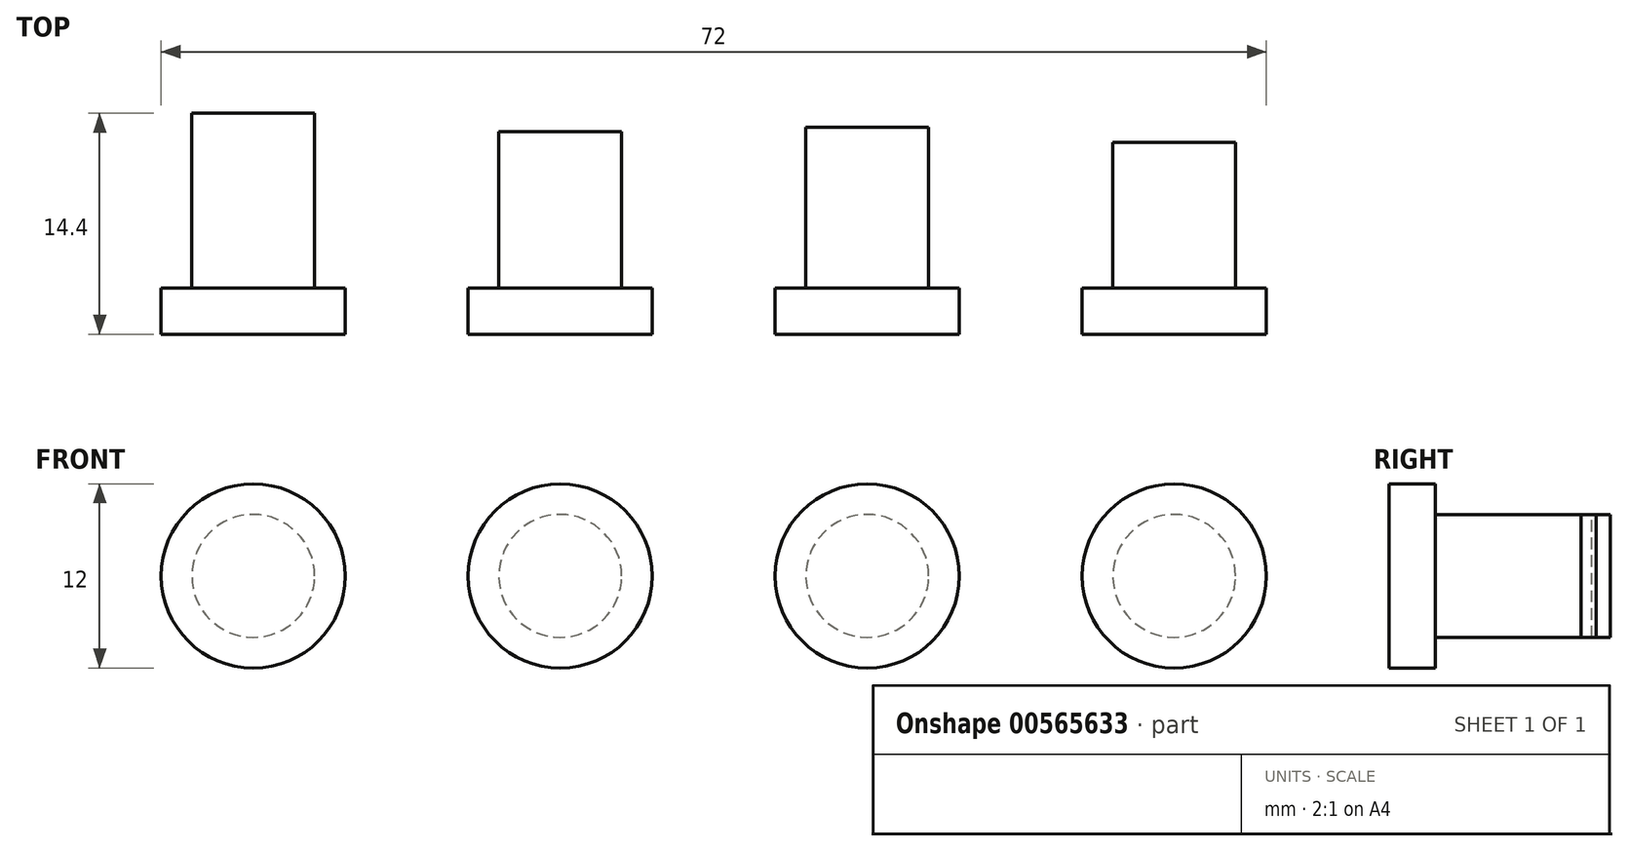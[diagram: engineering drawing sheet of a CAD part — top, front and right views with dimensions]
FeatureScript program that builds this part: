
annotation { "Feature Type Name" : "Feature", "Feature Type Description" : "" }
export const myFeature = defineFeature(function(context is Context, id is Id, definition is map)
    precondition{}
    {
        {
            var Q0;
            Q0=qCreatedBy(makeId("Front.planeOp"),FACE);
            var sketch = newSketch(context, id + "F0", { "sketchPlane" : qUnion([Q0])});
            skLineSegment(sketch, "E0", {"start": v(-7.35, 0) * mm, "end": v(7.35, 0) * mm, "construction": true});
            skLineSegment(sketch, "E1", {"start": v(0, 7.35) * mm, "end": v(0, -7.35) * mm, "construction": true});
            skPoint(sketch, "E2", {"position": v(0, 0) * mm});
            skCircle(sketch, "E3", {"center": v(0, 0) * mm, "radius": 4 * mm});
            skCircle(sketch, "E4", {"center": v(0, 0) * mm, "radius": 0.8 * mm, "construction": true});
            skLineSegment(sketch, "E5", {"start": v(18.77, 0) * mm, "end": v(101.23, 0) * mm, "construction": true});
            skLineSegment(sketch, "E6", {"start": v(60, 7.35) * mm, "end": v(60, -7.35) * mm, "construction": true});
            skPoint(sketch, "E7", {"position": v(60, 0) * mm});
            skCircle(sketch, "E8", {"center": v(60, 0) * mm, "radius": 4 * mm});
            skCircle(sketch, "E9", {"center": v(60, 0) * mm, "radius": 0.8 * mm, "construction": true});
            skLineSegment(sketch, "E10", {"start": v(9.1, 0) * mm, "end": v(70.9, 0) * mm, "construction": true});
            skLineSegment(sketch, "E11", {"start": v(40, 7.35) * mm, "end": v(40, -7.35) * mm, "construction": true});
            skPoint(sketch, "E12", {"position": v(40, 0) * mm});
            skCircle(sketch, "E13", {"center": v(40, 0) * mm, "radius": 4 * mm});
            skCircle(sketch, "E14", {"center": v(40, 0) * mm, "radius": 0.8 * mm, "construction": true});
            skLineSegment(sketch, "E15", {"start": v(7.93, 0) * mm, "end": v(32.07, 0) * mm, "construction": true});
            skLineSegment(sketch, "E16", {"start": v(20, 7.35) * mm, "end": v(20, -7.35) * mm, "construction": true});
            skPoint(sketch, "E17", {"position": v(20, 0) * mm});
            skCircle(sketch, "E18", {"center": v(20, 0) * mm, "radius": 4 * mm});
            skCircle(sketch, "E19", {"center": v(20, 0) * mm, "radius": 0.8 * mm, "construction": true});
            skLineSegment(sketch, "E20", {"start": v(0, 0) * mm, "end": v(20, 0) * mm, "construction": true});
            skLineSegment(sketch, "E21", {"start": v(20, 0) * mm, "end": v(40, 0) * mm, "construction": true});
            skLineSegment(sketch, "E22", {"start": v(40, 0) * mm, "end": v(60, 0) * mm, "construction": true});
            skCircle(sketch, "E23", {"center": v(0, 0) * mm, "radius": 6 * mm});
            skCircle(sketch, "E24", {"center": v(20, 0) * mm, "radius": 6 * mm});
            skCircle(sketch, "E25", {"center": v(40, 0) * mm, "radius": 6 * mm});
            skCircle(sketch, "E26", {"center": v(60, 0) * mm, "radius": 6 * mm});
            skSolve(sketch);
        }
        {
            var Q0;
            Q0=makeQuery(id+"F0.imprint","IMPRINT",FACE,{"disambiguationData":[TD([[makeQuery(id+"F0.imprint","IMPRINT",EDGE,{"derivedFrom":sQuery(id+"F0.wireOp",EDGE,"E3")}),1.0]])]});
            extrude(context, id + "F1", {"entities" : qUnion([Q0]), "oppositeDirection" : true, "depth" : 14.4 * mm, "offsetDistance" : 25 * mm});
        }
        {
            var Q0;
            Q0=makeQuery(id+"F0.imprint","IMPRINT",FACE,{"disambiguationData":[TD([[makeQuery(id+"F0.imprint","IMPRINT",EDGE,{"derivedFrom":sQuery(id+"F0.wireOp",EDGE,"E18")}),1.0]])]});
            extrude(context, id + "F2", {"entities" : qUnion([Q0]), "oppositeDirection" : true, "depth" : 13.2 * mm, "offsetDistance" : 25 * mm});
        }
        {
            var Q0;
            Q0=makeQuery(id+"F0.imprint","IMPRINT",FACE,{"disambiguationData":[TD([[makeQuery(id+"F0.imprint","IMPRINT",EDGE,{"derivedFrom":sQuery(id+"F0.wireOp",EDGE,"E13")}),1.0]])]});
            extrude(context, id + "F3", {"entities" : qUnion([Q0]), "oppositeDirection" : true, "depth" : 13.5 * mm, "offsetDistance" : 25 * mm});
        }
        {
            var Q0;
            Q0=makeQuery(id+"F0.imprint","IMPRINT",FACE,{"disambiguationData":[TD([[makeQuery(id+"F0.imprint","IMPRINT",EDGE,{"derivedFrom":sQuery(id+"F0.wireOp",EDGE,"E8")}),1.0]])]});
            extrude(context, id + "F4", {"entities" : qUnion([Q0]), "oppositeDirection" : true, "depth" : 12.5 * mm, "offsetDistance" : 25 * mm});
        }
        {
            var Q0;
            Q0=makeQuery(id+"F0.imprint","IMPRINT",FACE,{"disambiguationData":[TD([[makeQuery(id+"F0.imprint","IMPRINT",EDGE,{"derivedFrom":sQuery(id+"F0.wireOp",EDGE,"E13")}),-1.0]])]});
            var Q1;
            Q1=makeQuery(id+"F0.imprint","IMPRINT",FACE,{"disambiguationData":[TD([[makeQuery(id+"F0.imprint","IMPRINT",EDGE,{"derivedFrom":sQuery(id+"F0.wireOp",EDGE,"E18")}),-1.0]])]});
            var Q2;
            Q2=makeQuery(id+"F0.imprint","IMPRINT",FACE,{"disambiguationData":[TD([[makeQuery(id+"F0.imprint","IMPRINT",EDGE,{"derivedFrom":sQuery(id+"F0.wireOp",EDGE,"E3")}),-1.0]])]});
            var Q3;
            Q3=makeQuery(id+"F0.imprint","IMPRINT",FACE,{"disambiguationData":[TD([[makeQuery(id+"F0.imprint","IMPRINT",EDGE,{"derivedFrom":sQuery(id+"F0.wireOp",EDGE,"E8")}),-1.0]])]});
            extrude(context, id + "F5", {"entities" : qUnion([Q0, Q1, Q2, Q3]), "operationType" : NewBodyOperationType.ADD, "oppositeDirection" : true, "depth" : 3 * mm, "offsetDistance" : 25 * mm});
        }
    });
